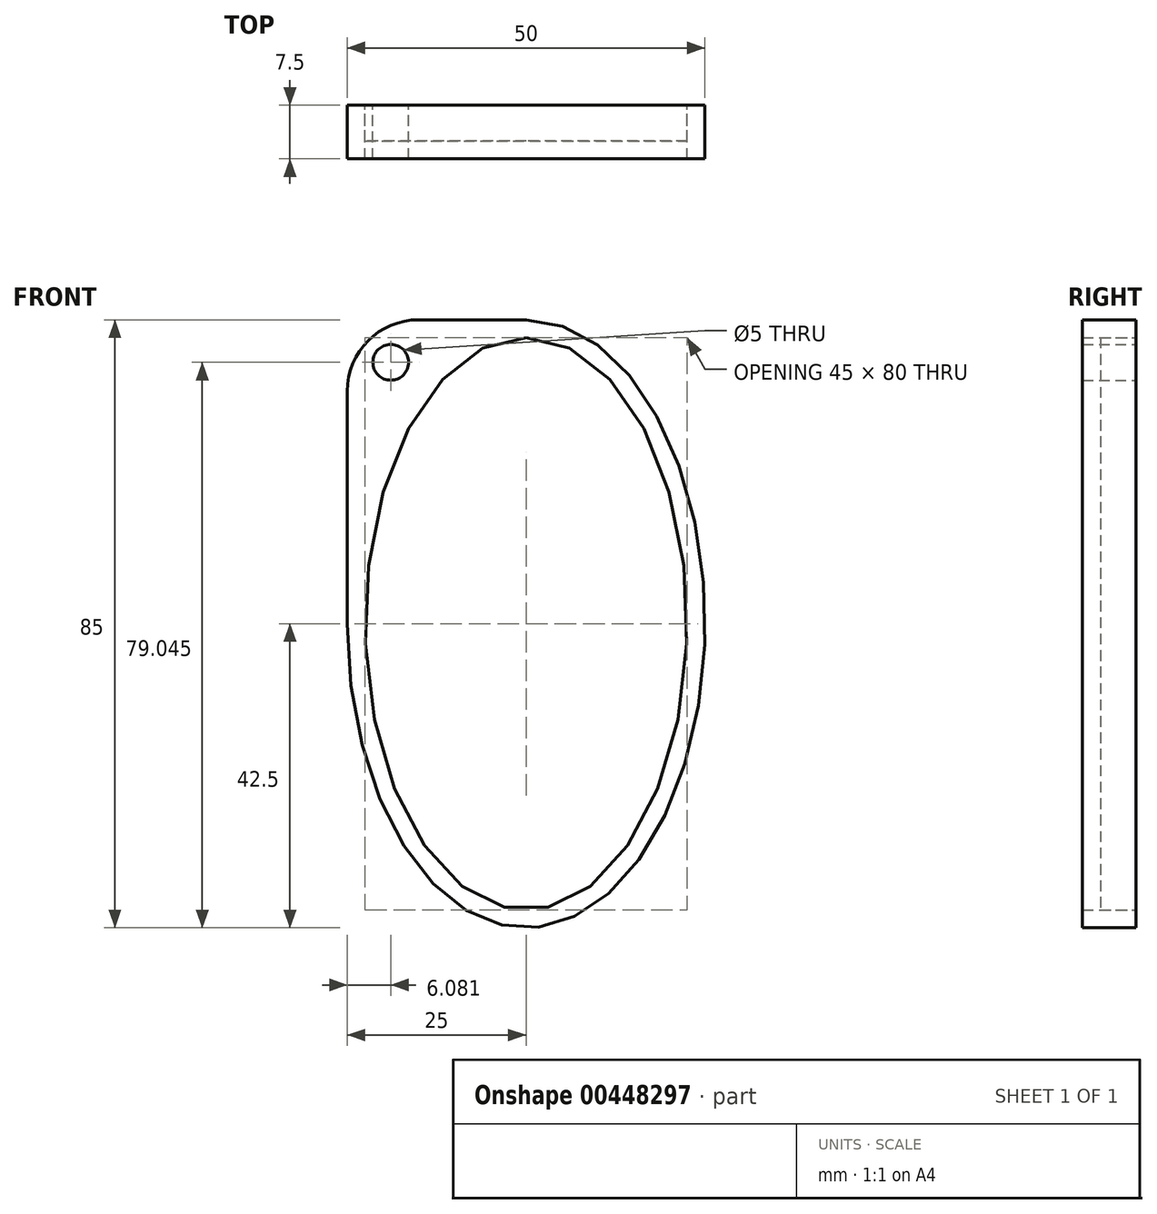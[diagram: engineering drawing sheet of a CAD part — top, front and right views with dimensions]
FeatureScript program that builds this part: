
annotation { "Feature Type Name" : "Feature", "Feature Type Description" : "" }
export const myFeature = defineFeature(function(context is Context, id is Id, definition is map)
    precondition{}
    {
        {
            var Q0;
            Q0=qCreatedBy(makeId("Front.planeOp"),FACE);
            var sketch = newSketch(context, id + "F0", { "sketchPlane" : qUnion([Q0])});
            skEllipse(sketch, "E0", {"center": v(0, 0) * mm, "majorRadius": 42.5 * mm, "minorRadius": 25 * mm, "majorAxis": v(0, 1)});
            skLineSegment(sketch, "E1.bottom", {"start": v(-25, 0) * mm, "end": v(25, 0) * mm});
            skLineSegment(sketch, "E1.left", {"start": v(-25, 0) * mm, "end": v(-25, 32.5) * mm});
            skPoint(sketch, "E2.visualSharp", {"position": v(-25, 42.5) * mm});
            skArc(sketch, "E2.filletArc", {"start": v(-15, 42.5) * mm, "mid": v(-22.07, 39.57) * mm, "end": v(-25, 32.5) * mm});
            skLineSegment(sketch, "E3", {"start": v(-15, 42.5) * mm, "end": v(0, 42.5) * mm});
            skEllipse(sketch, "E4", {"center": v(0, 0) * mm, "majorRadius": 40 * mm, "minorRadius": 22.5 * mm, "majorAxis": v(0, 1)});
            skCircle(sketch, "E5", {"center": v(-18.92, 36.55) * mm, "radius": 2.5 * mm});
            skSolve(sketch);
        }
        {
            var Q0;
            {var subQ0=sQuery(id+"F0.wireOp",EDGE,"E4");var subQ1=sQuery(id+"F0.wireOp",EDGE,"E1.bottom");var subQ2=makeQuery(id+"F0.imprint","INTERSECT",VERTEX,{"disambiguationData":[OD(0.0)],"derivedFrom":[subQ1,subQ0]});Q0=makeQuery(id+"F0.imprint","IMPRINT",FACE,{"disambiguationData":[TD([[makeQuery(id+"F0.imprint","IMPRINT",EDGE,{"disambiguationData":[TD([[subQ2,-1.0]])],"derivedFrom":subQ1}),1.0]])]});}
            var Q1;
            {var subQ0=sQuery(id+"F0.wireOp",EDGE,"E4");var subQ1=sQuery(id+"F0.wireOp",EDGE,"E1.bottom");var subQ2=makeQuery(id+"F0.imprint","INTERSECT",VERTEX,{"disambiguationData":[OD(0.0)],"derivedFrom":[subQ1,subQ0]});Q1=makeQuery(id+"F0.imprint","IMPRINT",FACE,{"disambiguationData":[TD([[makeQuery(id+"F0.imprint","IMPRINT",EDGE,{"disambiguationData":[TD([[subQ2,-1.0]])],"derivedFrom":subQ1}),-1.0]])]});}
            extrude(context, id + "F1", {"entities" : qUnion([Q0, Q1]), "depth" : 5 * mm});
        }
        {
            var Q0;
            {var subQ1=sQuery(id+"F0.wireOp",EDGE,"E1.left");Q0=makeQuery(id+"F0.imprint","IMPRINT",FACE,{"disambiguationData":[TD([[makeQuery(id+"F0.imprint","IMPRINT",EDGE,{"derivedFrom":subQ1}),-1.0]])]});}
            var Q1;
            {var subQ0=sQuery(id+"F0.wireOp",EDGE,"E1.bottom");var subQ1=sQuery(id+"F0.wireOp",EDGE,"E0");var subQ3=makeQuery(id+"F0.imprint","INTERSECT",VERTEX,{"derivedFrom":[subQ1,subQ0]});Q1=makeQuery(id+"F0.imprint","IMPRINT",FACE,{"disambiguationData":[TD([[makeQuery(id+"F0.imprint","IMPRINT",EDGE,{"disambiguationData":[TD([[subQ3,1.0]])],"derivedFrom":subQ0}),-1.0]])]});}
            var Q2;
            {var subQ0=sQuery(id+"F0.wireOp",EDGE,"E1.bottom");var subQ1=sQuery(id+"F0.wireOp",EDGE,"E0");var subQ5=makeQuery(id+"F0.imprint","INTERSECT",VERTEX,{"derivedFrom":[subQ1,subQ0]});Q2=makeQuery(id+"F0.imprint","IMPRINT",FACE,{"disambiguationData":[TD([[makeQuery(id+"F0.imprint","IMPRINT",EDGE,{"disambiguationData":[TD([[subQ5,-1.0]])],"derivedFrom":subQ1}),1.0]])]});}
            extrude(context, id + "F2", {"entities" : qUnion([Q0, Q1, Q2]), "depth" : 7.5 * mm});
        }
    });
